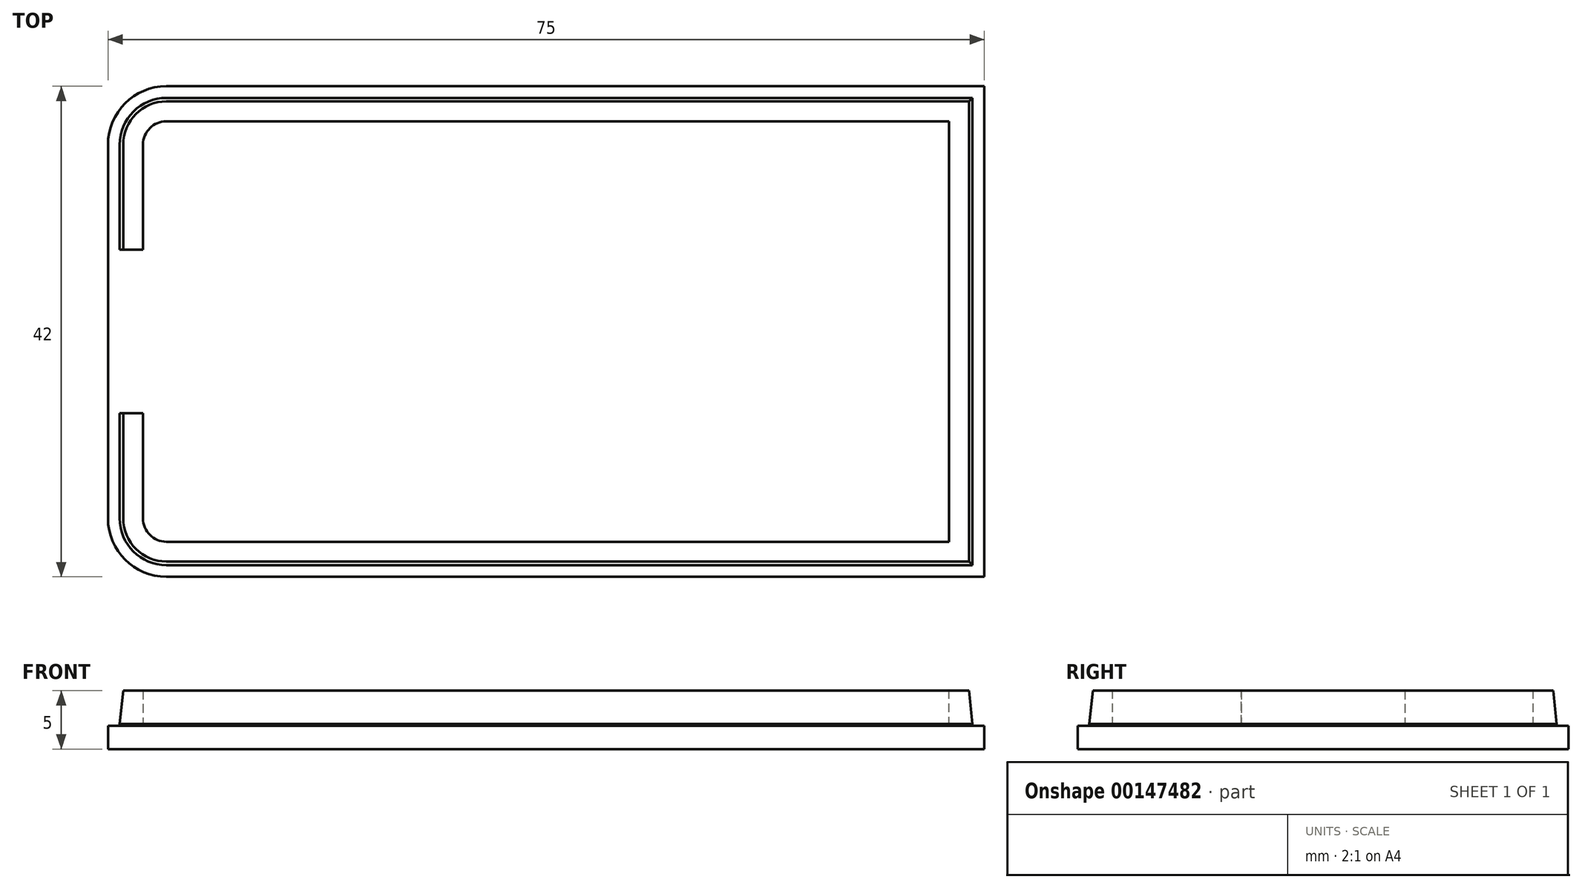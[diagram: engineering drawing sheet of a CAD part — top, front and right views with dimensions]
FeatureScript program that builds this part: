
annotation { "Feature Type Name" : "Feature", "Feature Type Description" : "" }
export const myFeature = defineFeature(function(context is Context, id is Id, definition is map)
    precondition{}
    {
        {
            var Q0;
            Q0=qCreatedBy(makeId("Top.planeOp"),FACE);
            var sketch = newSketch(context, id + "F0", { "sketchPlane" : qUnion([Q0])});
            skLineSegment(sketch, "E0.bottom", {"start": v(37.5, 21) * mm, "end": v(-32.5, 21) * mm});
            skLineSegment(sketch, "E0.top", {"start": v(37.5, -21) * mm, "end": v(-32.5, -21) * mm});
            skLineSegment(sketch, "E0.left", {"start": v(37.5, 21) * mm, "end": v(37.5, -21) * mm});
            skLineSegment(sketch, "E0.right", {"start": v(-37.5, 16) * mm, "end": v(-37.5, -16) * mm});
            skPoint(sketch, "E0.middle", {"position": v(0, 0) * mm});
            skPoint(sketch, "E1.visualSharp", {"position": v(-37.5, 21) * mm});
            skArc(sketch, "E1.filletArc", {"start": v(-32.5, 21) * mm, "mid": v(-36.04, 19.54) * mm, "end": v(-37.5, 16) * mm});
            skPoint(sketch, "E2.visualSharp", {"position": v(-37.5, -21) * mm});
            skArc(sketch, "E2.filletArc", {"start": v(-37.5, -16) * mm, "mid": v(-36.04, -19.54) * mm, "end": v(-32.5, -21) * mm});
            skSolve(sketch);
        }
        {
            var Q0;
            Q0=makeQuery(id+"F0.imprint","IMPRINT",FACE,{"disambiguationData":[TD([[makeQuery(id+"F0.imprint","IMPRINT",EDGE,{"derivedFrom":sQuery(id+"F0.wireOp",EDGE,"E0.bottom")}),1.0]])]});
            extrude(context, id + "F1", {"entities" : qUnion([Q0]), "depth" : 2 * mm});
        }
        {
            var Q0;
            Q0=qCreatedBy(makeId("Top.planeOp"),FACE);
            var sketch = newSketch(context, id + "F2", { "sketchPlane" : qUnion([Q0])});
            skLineSegment(sketch, "E3.0", {"start": v(-32.5, -20) * mm, "end": v(36.5, -20) * mm});
            skLineSegment(sketch, "E3.1", {"start": v(36.5, 20) * mm, "end": v(-32.5, 20) * mm});
            skArc(sketch, "E3.2", {"start": v(-32.5, 20) * mm, "mid": v(-35.33, 18.83) * mm, "end": v(-36.5, 16) * mm});
            skLineSegment(sketch, "E3.3", {"start": v(36.5, -20) * mm, "end": v(36.5, 20) * mm});
            skLineSegment(sketch, "E3.4", {"start": v(-36.5, 16) * mm, "end": v(-36.5, -16) * mm});
            skArc(sketch, "E3.5", {"start": v(-36.5, -16) * mm, "mid": v(-35.33, -18.83) * mm, "end": v(-32.5, -20) * mm});
            skSolve(sketch);
        }
        {
            var Q0;
            Q0 = qSketchRegion(id + "F2", true);
            extrude(context, id + "F3", {"entities" : qUnion([Q0]), "operationType" : NewBodyOperationType.ADD, "depth" : 5 * mm});
        }
        {
            var Q0;
            Q0=makeQuery(id+"F3.opExtrude","CAP_FACE",FACE,{"disambiguationData":[OSD([sQuery(id+"F2.wireOp",EDGE,"E3.0"),sQuery(id+"F2.wireOp",EDGE,"E3.1"),sQuery(id+"F2.wireOp",EDGE,"E3.2"),sQuery(id+"F2.wireOp",EDGE,"E3.3"),sQuery(id+"F2.wireOp",EDGE,"E3.4"),sQuery(id+"F2.wireOp",EDGE,"E3.5")])],"isStart":false});
            var sketch = newSketch(context, id + "F4", { "sketchPlane" : qUnion([Q0])});
            skLineSegment(sketch, "E4.0", {"start": v(-34.5, 16) * mm, "end": v(-34.5, -16) * mm});
            skLineSegment(sketch, "E4.1", {"start": v(-32.5, -18) * mm, "end": v(34.5, -18) * mm});
            skLineSegment(sketch, "E4.2", {"start": v(34.5, -18) * mm, "end": v(34.5, 18) * mm});
            skArc(sketch, "E4.3", {"start": v(-34.5, -16) * mm, "mid": v(-33.91, -17.41) * mm, "end": v(-32.5, -18) * mm});
            skLineSegment(sketch, "E4.4", {"start": v(34.5, 18) * mm, "end": v(-32.5, 18) * mm});
            skArc(sketch, "E4.5", {"start": v(-32.5, 18) * mm, "mid": v(-33.91, 17.41) * mm, "end": v(-34.5, 16) * mm});
            skSolve(sketch);
        }
        {
            var Q0;
            Q0 = qSketchRegion(id + "F4", true);
            extrude(context, id + "F5", {"entities" : qUnion([Q0]), "operationType" : NewBodyOperationType.REMOVE, "oppositeDirection" : true, "depth" : 3 * mm});
        }
        {
            var Q0;
            Q0=makeQuery(id+"F3.opExtrude","CAP_FACE",FACE,{"disambiguationData":[OSD([sQuery(id+"F2.wireOp",EDGE,"E3.0"),sQuery(id+"F2.wireOp",EDGE,"E3.1"),sQuery(id+"F2.wireOp",EDGE,"E3.2"),sQuery(id+"F2.wireOp",EDGE,"E3.3"),sQuery(id+"F2.wireOp",EDGE,"E3.4"),sQuery(id+"F2.wireOp",EDGE,"E3.5")])],"isStart":false});
            var sketch = newSketch(context, id + "F6", { "sketchPlane" : qUnion([Q0])});
            skLineSegment(sketch, "E5.bottom", {"start": v(-33.43, 7) * mm, "end": v(-36.96, 7) * mm});
            skLineSegment(sketch, "E5.top", {"start": v(-33.43, -7) * mm, "end": v(-36.96, -7) * mm});
            skLineSegment(sketch, "E5.left", {"start": v(-33.43, 7) * mm, "end": v(-33.43, -7) * mm});
            skLineSegment(sketch, "E5.right", {"start": v(-36.96, 7) * mm, "end": v(-36.96, -7) * mm});
            skPoint(sketch, "E5.middle", {"position": v(-35.2, 0) * mm});
            skPoint(sketch, "E5.middle.positionSnap0", {"position": v(-36.5, 0) * mm});
            skPoint(sketch, "E5.centerSnap0", {"position": v(-36.5, 0) * mm});
            skSolve(sketch);
        }
        {
            var Q0;
            Q0 = qSketchRegion(id + "F6", true);
            extrude(context, id + "F7", {"entities" : qUnion([Q0]), "operationType" : NewBodyOperationType.REMOVE, "oppositeDirection" : true, "depth" : 3 * mm});
        }
        {
            var Q0;
            {var subQ0=sQuery(id+"F2.wireOp",EDGE,"E3.5");var subQ1=sQuery(id+"F2.wireOp",EDGE,"E3.4");Q0=makeQuery(id+"F7.boolean.opBoolean","SPLIT",EDGE,{"disambiguationData":[TD([makeQuery(id+"F3.opExtrude","SWEPT_FACE",FACE,{"disambiguationData":[OSD([subQ0])]})])],"derivedFrom":makeQuery(id+"F3.opExtrude","CAP_EDGE",EDGE,{"disambiguationData":[OSD([subQ1])],"isStart":false})});}
            var Q1;
            Q1=makeQuery(id+"F3.opExtrude","CAP_EDGE",EDGE,{"disambiguationData":[OSD([sQuery(id+"F2.wireOp",EDGE,"E3.3")])],"isStart":false});
            var Q2;
            Q2=makeQuery(id+"F3.opExtrude","CAP_EDGE",EDGE,{"disambiguationData":[OSD([sQuery(id+"F2.wireOp",EDGE,"E3.1")])],"isStart":false});
            chamfer(context, id + "F8", {"entities" : qUnion([Q0, Q1, Q2]), "chamferType" : ChamferType.OFFSET_ANGLE, "width" : 0.3 * mm, "oppositeDirection" : false, "angle" : 84 * degree, "tangentPropagation" : true});
        }
    });
